# Revit family: Hager-Univers-IP30-D160-Cl.II-FWQ-encl-NoHosted-NL-en
name_source: partatom
category: Equipement électrique
units: mm (PartAtom-declared; Revit-internal decimal feet)

## family parameters
Basée sur le plan de construction = Oui
Configuration du panneau = Deux colonnes, circuits au sein
Cote de connecteur circulaire = Utiliser le diamètre
Couper avec des vides une fois chargée = Non
Partagée = Non
Point de calcul de pièce = Non
Toujours verticalement = Oui
Type d'élément = Tableau de raccordement

## types (20) — shared parameters
Commentaires du type = Univers
EF000003 - Mounting method = EV000384 - Surface mounted (plaster)
EF000007 - Colour = EV000202 - White
EF000049 - Depth = 160 mm  [stored 0.524934 ft]
EF000116 - RAL-number = 9010
EF001088 - Extension possible = Oui
EF001596 - Material housing = EV000179 - Steel
EF001613 - Circuit integrity = EV000494 - None
EF003532 - Suitable for outdoor use = Non
EF005474 - Degree of protection (IP) = EV006410 - IP30
EF006244 - Transparent cover/door = Non
EF006306 - With lock = Non
EF007800 - Suitable for lightning protection = Non
EF008873 - Nominal current (In) = 125 A
EF009170 - Material plate thickness cabinet = 2 mm  [stored 0.00656168 ft]
EF009171 - Material plate thickness door/cover = 2 mm  [stored 0.00656168 ft]
EF009212 - Cover model = EV009916 - With notch
EF015940 - Cover with overpressure release = Non
Elévation par défaut = 1219 mm
Fabricant = Hager
HG000002 - With door or cover = Non
HG000003 - Range = Univers
HG000006 - Flush mounted = Non
HG000009 - Double swing door = Non
HG000010 - Asymmetric doors = Non
HG000023 - Double section enclosure = Non
HG000024 - Bottom section height = 600 mm
HG000026 - Floor standing = Non
zero-valued in all types: EF000218 - Built-in depth, HG000027 - Plinth height

## per-type parameters (varying)
| type | EF000008 - Width | EF000040 - Height | EF000118 - With mounting plate | EF000266 - Number of rows | EF000339 - Type of cover | EF000437 - Number of conduit inlets | EF001131 - Internal depth | EF002950 - Width in number of modular spacings | EF004293 - Impact strength | EF004427 - Number of modules | EF004464 - Type of door | EF009554 - Number of openings for flange plates | HG000004 - Manufacturer reference |
| Surface mounted (plaster) IP30 W1050 H1100 D160  - FWQ74N1 | 1050 mm | 1100 mm | Oui | 7 | EV001012 - Cover | 16 | 160 mm  [stored 0.524934 ft] | 48 | EV006815 - IK09 | 336 | EV002646 - Single | 8 | FWQ74N1 |
| Surface mounted (plaster) IP30 W1050 H650 D160  - FWQ34D1 | 1050 mm | 650 mm  [stored 2.13255 ft] | Oui | 16 | EV001012 - Cover | 16 | 160 mm  [stored 0.524934 ft] | 48 | EV006815 - IK09 | 192 | EV002646 - Single | 8 | FWQ34D1 |
| Surface mounted (plaster) IP30 W1050 H650 D160  - FWQ44D1 | 1050 mm | 650 mm  [stored 2.13255 ft] | Oui | 16 | EV001012 - Cover | 16 | 160 mm  [stored 0.524934 ft] | 48 |  | 192 | EV002646 - Single | 8 | FWQ44D1 |
| Surface mounted (plaster) IP30 W1050 H800 D160  - FWQ54D1 | 1050 mm | 800 mm  [stored 2.62467 ft] | Oui | 20 | EV001012 - Cover | 16 | 160 mm  [stored 0.524934 ft] | 48 |  | 240 | EV002646 - Single | 8 | FWQ54D1 |
| Surface mounted (plaster) IP30 W300 H650 D160  - FWQ41D1 | 300 mm | 650 mm  [stored 2.13255 ft] | Oui | 4 | EV001012 - Cover | 4 | 160 mm  [stored 0.524934 ft] | 12 |  | 48 | EV002646 - Single | 2 | FWQ41D1 |
| Surface mounted (plaster) IP30 W300 H950 D160  - FWQ61D1 | 300 mm | 950 mm  [stored 3.1168 ft] | Oui | 6 | EV001012 - Cover | 4 | 160 mm  [stored 0.524934 ft] | 12 |  | 72 | EV002646 - Single | 2 | FWQ61D1 |
| Surface mounted (plaster) IP30 W550 H1100 D160  - FWQ72D1 | 550 mm | 1100 mm | Oui | 14 | EV001012 - Cover | 8 | 160 mm  [stored 0.524934 ft] | 12 |  | 168 | EV002646 - Single | 4 | FWQ72D1 |
| Surface mounted (plaster) IP30 W550 H1100 D160  - FWQ72N1 | 550 mm | 1100 mm | Oui | 7 | EV001012 - Cover | 8 | 160 mm  [stored 0.524934 ft] | 24 | EV006815 - IK09 | 168 | EV002646 - Single | 4 | FWQ72N1 |
| Surface mounted (plaster) IP30 W550 H650 D160  - FWQ42D1 | 550 mm | 650 mm  [stored 2.13255 ft] | Oui | 8 | EV001012 - Cover | 8 | 160 mm  [stored 0.524934 ft] | 24 |  | 96 | EV002646 - Single | 4 | FWQ42D1 |
| Surface mounted (plaster) IP30 W550 H800 D160  - FWQ52D1 | 550 mm | 800 mm  [stored 2.62467 ft] | Oui | 10 | EV001012 - Cover | 8 | 160 mm  [stored 0.524934 ft] | 24 |  | 120 | EV002646 - Single | 4 | FWQ52D1 |
| Surface mounted (plaster) IP30 W550 H800 D160  - FWQ52N1 | 550 mm | 800 mm  [stored 2.62467 ft] | Oui | 5 | EV001012 - Cover | 8 | 160 mm  [stored 0.524934 ft] | 24 | EV006815 - IK09 | 120 | EV002646 - Single | 4 | FWQ52N1 |
| Surface mounted (plaster) IP30 W550 H950 D160  - FWQ62D1 | 550 mm | 950 mm  [stored 3.1168 ft] | Oui | 12 | EV001012 - Cover | 8 | 160 mm  [stored 0.524934 ft] | 24 |  | 144 | EV002646 - Single | 4 | FWQ62D1 |
| Surface mounted (plaster) IP30 W550 H950 D160  - FWQ62N1 | 550 mm | 950 mm  [stored 3.1168 ft] | Oui | 2 | EV001012 - Cover | 8 | 160 mm  [stored 0.524934 ft] | 24 | EV006815 - IK09 | 96 | EV002646 - Single | 4 | FWQ62N1 |
| Surface mounted (plaster) IP30 W800 H1100 D160  - FWQ73N1 | 800 mm  [stored 2.62467 ft] | 1100 mm | Oui | 7 | EV001012 - Cover | 12 | 160 mm  [stored 0.524934 ft] | 36 | EV006815 - IK09 | 252 | EV002646 - Single | 6 | FWQ73N1 |
| Surface mounted (plaster) IP30 W800 H500 D160  - FWQ33D1 | 800 mm  [stored 2.62467 ft] | 500 mm  [stored 1.64042 ft] | Non | 9 | EV000494 - None | 12 | 156 mm  [stored 0.511811 ft] | 36 |  | 108 | EV000494 - None | 6 | FWQ33D1 |
| Surface mounted (plaster) IP30 W800 H650 D160  - FWQ43D1 | 800 mm  [stored 2.62467 ft] | 650 mm  [stored 2.13255 ft] | Oui | 12 | EV001012 - Cover | 12 | 160 mm  [stored 0.524934 ft] | 36 |  | 144 | EV002646 - Single | 6 | FWQ43D1 |
| Surface mounted (plaster) IP30 W800 H800 D160  - FWQ53D1 | 800 mm  [stored 2.62467 ft] | 800 mm  [stored 2.62467 ft] | Oui | 15 | EV001012 - Cover | 12 | 160 mm  [stored 0.524934 ft] | 36 |  | 180 | EV002646 - Single | 6 | FWQ53D1 |
| Surface mounted (plaster) IP30 W800 H800 D160  - FWQ53N1 | 800 mm  [stored 2.62467 ft] | 800 mm  [stored 2.62467 ft] | Oui | 5 | EV001012 - Cover | 12 | 160 mm  [stored 0.524934 ft] | 36 | EV006815 - IK09 | 180 | EV002646 - Single | 6 | FWQ53N1 |
| Surface mounted (plaster) IP30 W800 H950 D160  - FWQ63D1 | 800 mm  [stored 2.62467 ft] | 950 mm  [stored 3.1168 ft] | Oui | 18 | EV001012 - Cover | 12 | 160 mm  [stored 0.524934 ft] | 36 |  | 216 | EV002646 - Single | 6 | FWQ63D1 |
| Surface mounted (plaster) IP30 W800 H950 D160  - FWQ63N1 | 800 mm  [stored 2.62467 ft] | 950 mm  [stored 3.1168 ft] | Oui | 3 | EV001012 - Cover | 12 | 160 mm  [stored 0.524934 ft] | 36 | EV006815 - IK09 | 144 | EV002646 - Single | 6 | FWQ63N1 |

note: [stored X ft] marks values corroborated as IEEE doubles in the binary element streams (Revit-internal decimal feet)

## geometry (parser evidence)
native form markers: Blend x4, Sweep x10
no freeform markers — native parametric forms only
